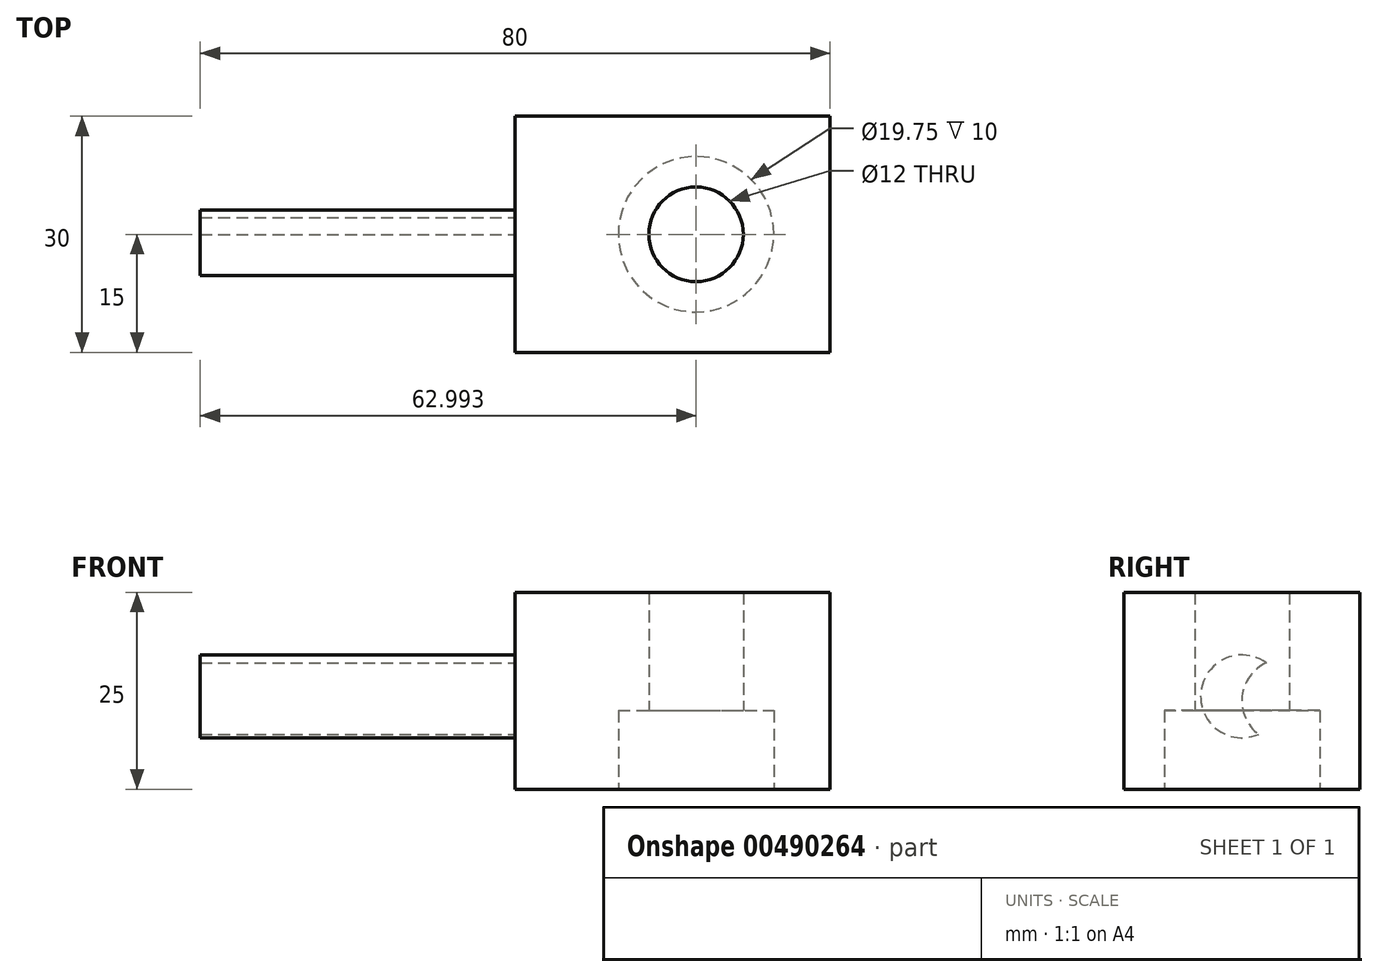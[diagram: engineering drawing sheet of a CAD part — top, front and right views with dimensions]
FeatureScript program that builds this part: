
annotation { "Feature Type Name" : "Feature", "Feature Type Description" : "" }
export const myFeature = defineFeature(function(context is Context, id is Id, definition is map)
    precondition{}
    {
        {
            var Q0;
            Q0=qCreatedBy(makeId("Top.planeOp"),FACE);
            var sketch = newSketch(context, id + "F0", { "sketchPlane" : qUnion([Q0])});
            skLineSegment(sketch, "E0.bottom", {"start": v(-13.12, 15) * mm, "end": v(26.88, 15) * mm});
            skLineSegment(sketch, "E0.top", {"start": v(-13.12, -15) * mm, "end": v(26.88, -15) * mm});
            skLineSegment(sketch, "E0.left", {"start": v(-13.12, 15) * mm, "end": v(-13.12, -15) * mm});
            skLineSegment(sketch, "E0.right", {"start": v(26.88, 15) * mm, "end": v(26.88, -15) * mm});
            skSolve(sketch);
        }
        {
            var Q0;
            Q0 = qSketchRegion(id + "F0", true);
            extrude(context, id + "F1", {"entities" : qUnion([Q0]), "depth" : 25 * mm});
        }
        {
            var Q0;
            Q0=makeQuery(id+"F1.opExtrude","CAP_FACE",FACE,{"disambiguationData":[OSD([sQuery(id+"F0.wireOp",EDGE,"E0.bottom"),sQuery(id+"F0.wireOp",EDGE,"E0.top"),sQuery(id+"F0.wireOp",EDGE,"E0.left"),sQuery(id+"F0.wireOp",EDGE,"E0.right")])],"isStart":true});
            var sketch = newSketch(context, id + "F2", { "sketchPlane" : qUnion([Q0])});
            skCircle(sketch, "E1", {"center": v(9.87, 0) * mm, "radius": 9.87 * mm});
            skSolve(sketch);
        }
        {
            var Q0;
            Q0=makeQuery(id+"F2.imprint","IMPRINT",FACE,{"disambiguationData":[TD([[makeQuery(id+"F2.imprint","IMPRINT",EDGE,{"derivedFrom":sQuery(id+"F2.wireOp",EDGE,"E1")}),1.0]])]});
            extrude(context, id + "F3", {"entities" : qUnion([Q0]), "operationType" : NewBodyOperationType.REMOVE, "oppositeDirection" : true, "depth" : 10 * mm});
        }
        {
            var Q0;
            Q0=makeQuery(id+"F3.boolean.opBoolean","COPY",FACE,{"derivedFrom":makeQuery(id+"F3.opExtrude","CAP_FACE",FACE,{"disambiguationData":[OSD([sQuery(id+"F2.wireOp",EDGE,"E1")])],"isStart":false})});
            var sketch = newSketch(context, id + "F4", { "sketchPlane" : qUnion([Q0])});
            skCircle(sketch, "E2", {"center": v(9.87, 0) * mm, "radius": 6 * mm});
            skSolve(sketch);
        }
        {
            var Q0;
            Q0=makeQuery(id+"F4.imprint","IMPRINT",FACE,{"disambiguationData":[TD([[makeQuery(id+"F4.imprint","IMPRINT",EDGE,{"derivedFrom":sQuery(id+"F4.wireOp",EDGE,"E2")}),1.0]])]});
            extrude(context, id + "F5", {"entities" : qUnion([Q0]), "operationType" : NewBodyOperationType.REMOVE, "oppositeDirection" : true, "depth" : 25 * mm});
        }
        {
            var Q0;
            Q0=makeQuery(id+"F1.opExtrude","SWEPT_FACE",FACE,{"disambiguationData":[OSD([sQuery(id+"F0.wireOp",EDGE,"E0.left")])]});
            var sketch = newSketch(context, id + "F6", { "sketchPlane" : qUnion([Q0])});
            skCircle(sketch, "E3", {"center": v(0, 11.8) * mm, "radius": 5.26 * mm});
            skCircle(sketch, "E4", {"center": v(-5.23, 11.23) * mm, "radius": 5.26 * mm});
            skSolve(sketch);
        }
        {
            var Q0;
            {var subQ0=sQuery(id+"F6.wireOp",EDGE,"E4");var subQ1=sQuery(id+"F6.wireOp",EDGE,"E3");var subQ2=makeQuery(id+"F6.imprint","INTERSECT",VERTEX,{"disambiguationData":[OD(0.0)],"derivedFrom":[subQ1,subQ0]});Q0=makeQuery(id+"F6.imprint","IMPRINT",FACE,{"disambiguationData":[TD([[makeQuery(id+"F6.imprint","IMPRINT",EDGE,{"disambiguationData":[TD([[subQ2,-1.0]])],"derivedFrom":subQ1}),1.0]])]});}
            extrude(context, id + "F7", {"entities" : qUnion([Q0]), "operationType" : NewBodyOperationType.ADD, "depth" : 40 * mm});
        }
    });
